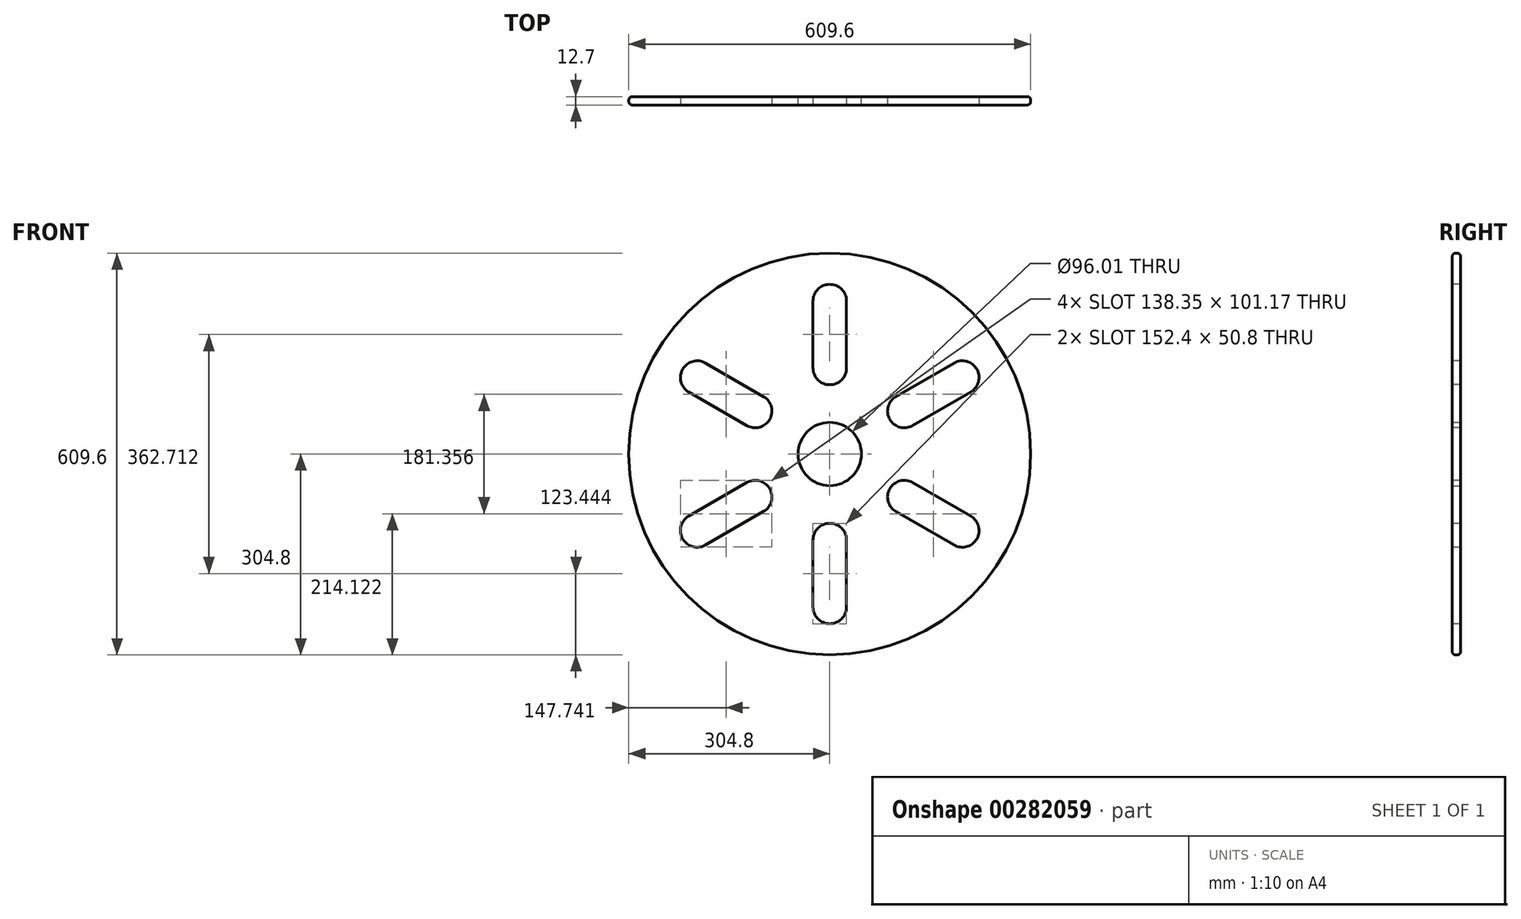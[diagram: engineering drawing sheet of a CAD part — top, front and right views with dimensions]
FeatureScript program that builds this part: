
annotation { "Feature Type Name" : "Feature", "Feature Type Description" : "" }
export const myFeature = defineFeature(function(context is Context, id is Id, definition is map)
    precondition{}
    {
        {
            var Q0;
            Q0=qCreatedBy(makeId("Front.planeOp"),FACE);
            var sketch = newSketch(context, id + "F0", { "sketchPlane" : qUnion([Q0])});
            skCircle(sketch, "E0", {"center": v(0, 0) * mm, "radius": 304.8 * mm});
            skCircle(sketch, "E1", {"center": v(0, 0) * mm, "radius": 48 * mm});
            skSolve(sketch);
        }
        {
            var Q0;
            Q0=makeQuery(id+"F0.imprint","IMPRINT",FACE,{"disambiguationData":[TD([[makeQuery(id+"F0.imprint","IMPRINT",EDGE,{"derivedFrom":sQuery(id+"F0.wireOp",EDGE,"E0")}),1.0]])]});
            extrude(context, id + "F1", {"entities" : qUnion([Q0]), "depth" : 12.7 * mm});
        }
        {
            var Q0;
            Q0=makeQuery(id+"F1.opExtrude","CAP_FACE",FACE,{"disambiguationData":[OSD([sQuery(id+"F0.wireOp",EDGE,"E0"),sQuery(id+"F0.wireOp",EDGE,"E1")])],"isStart":false});
            var sketch = newSketch(context, id + "F2", { "sketchPlane" : qUnion([Q0])});
            skLineSegment(sketch, "E2.left", {"start": v(-25.4, 130.56) * mm, "end": v(-25.4, 232.16) * mm});
            skLineSegment(sketch, "E2.right", {"start": v(25.4, 130.56) * mm, "end": v(25.4, 232.16) * mm});
            skPoint(sketch, "E2.middle", {"position": v(0, 181.36) * mm});
            skArc(sketch, "E3", {"start": v(25.4, 232.16) * mm, "mid": v(0, 257.56) * mm, "end": v(-25.4, 232.16) * mm});
            skArc(sketch, "E4", {"start": v(-25.4, 130.56) * mm, "mid": v(0, 105.16) * mm, "end": v(25.4, 130.56) * mm});
            skArc(sketch, "E5.1.0", {"start": v(-125.76, 43.28) * mm, "mid": v(-91.07, 52.58) * mm, "end": v(-100.36, 87.28) * mm});
            skLineSegment(sketch, "E5.1.1", {"start": v(-100.36, 87.28) * mm, "end": v(-188.35, 138.08) * mm});
            skLineSegment(sketch, "E5.1.2", {"start": v(-125.76, 43.28) * mm, "end": v(-213.75, 94.08) * mm});
            skArc(sketch, "E5.1.3", {"start": v(-188.35, 138.08) * mm, "mid": v(-223.05, 128.78) * mm, "end": v(-213.75, 94.08) * mm});
            skArc(sketch, "E5.2.0", {"start": v(-100.36, -87.28) * mm, "mid": v(-91.07, -52.58) * mm, "end": v(-125.76, -43.28) * mm});
            skLineSegment(sketch, "E5.2.1", {"start": v(-125.76, -43.28) * mm, "end": v(-213.75, -94.08) * mm});
            skLineSegment(sketch, "E5.2.2", {"start": v(-100.36, -87.28) * mm, "end": v(-188.35, -138.08) * mm});
            skArc(sketch, "E5.2.3", {"start": v(-213.75, -94.08) * mm, "mid": v(-223.05, -128.78) * mm, "end": v(-188.35, -138.08) * mm});
            skArc(sketch, "E5.3.0", {"start": v(25.4, -130.56) * mm, "mid": v(0, -105.16) * mm, "end": v(-25.4, -130.56) * mm});
            skLineSegment(sketch, "E5.3.1", {"start": v(-25.4, -130.56) * mm, "end": v(-25.4, -232.16) * mm});
            skLineSegment(sketch, "E5.3.2", {"start": v(25.4, -130.56) * mm, "end": v(25.4, -232.16) * mm});
            skArc(sketch, "E5.3.3", {"start": v(-25.4, -232.16) * mm, "mid": v(0, -257.56) * mm, "end": v(25.4, -232.16) * mm});
            skArc(sketch, "E5.4.0", {"start": v(125.76, -43.28) * mm, "mid": v(91.07, -52.58) * mm, "end": v(100.36, -87.28) * mm});
            skLineSegment(sketch, "E5.4.1", {"start": v(100.36, -87.28) * mm, "end": v(188.35, -138.08) * mm});
            skLineSegment(sketch, "E5.4.2", {"start": v(125.76, -43.28) * mm, "end": v(213.75, -94.08) * mm});
            skArc(sketch, "E5.4.3", {"start": v(188.35, -138.08) * mm, "mid": v(223.05, -128.78) * mm, "end": v(213.75, -94.08) * mm});
            skArc(sketch, "E5.5.0", {"start": v(100.36, 87.28) * mm, "mid": v(91.07, 52.58) * mm, "end": v(125.76, 43.28) * mm});
            skLineSegment(sketch, "E5.5.1", {"start": v(125.76, 43.28) * mm, "end": v(213.75, 94.08) * mm});
            skLineSegment(sketch, "E5.5.2", {"start": v(100.36, 87.28) * mm, "end": v(188.35, 138.08) * mm});
            skArc(sketch, "E5.5.3", {"start": v(213.75, 94.08) * mm, "mid": v(223.05, 128.78) * mm, "end": v(188.35, 138.08) * mm});
            skPoint(sketch, "E5.center", {"position": v(0, 0) * mm});
            skLineSegment(sketch, "E6", {"start": v(0, 304.8) * mm, "end": v(0, -304.8) * mm, "construction": true});
            skSolve(sketch);
        }
        {
            var Q0;
            Q0=makeQuery(id+"F2.imprint","IMPRINT",FACE,{"disambiguationData":[TD([[makeQuery(id+"F2.imprint","IMPRINT",EDGE,{"derivedFrom":sQuery(id+"F2.wireOp",EDGE,"E2.left")}),-1.0]])]});
            var Q1;
            Q1=makeQuery(id+"F2.imprint","IMPRINT",FACE,{"disambiguationData":[TD([[makeQuery(id+"F2.imprint","IMPRINT",EDGE,{"derivedFrom":sQuery(id+"F2.wireOp",EDGE,"E5.5.0")}),1.0]])]});
            var Q2;
            Q2=makeQuery(id+"F2.imprint","IMPRINT",FACE,{"disambiguationData":[TD([[makeQuery(id+"F2.imprint","IMPRINT",EDGE,{"derivedFrom":sQuery(id+"F2.wireOp",EDGE,"E5.4.0")}),1.0]])]});
            var Q3;
            Q3=makeQuery(id+"F2.imprint","IMPRINT",FACE,{"disambiguationData":[TD([[makeQuery(id+"F2.imprint","IMPRINT",EDGE,{"derivedFrom":sQuery(id+"F2.wireOp",EDGE,"E5.3.0")}),1.0]])]});
            var Q4;
            Q4=makeQuery(id+"F2.imprint","IMPRINT",FACE,{"disambiguationData":[TD([[makeQuery(id+"F2.imprint","IMPRINT",EDGE,{"derivedFrom":sQuery(id+"F2.wireOp",EDGE,"E5.2.0")}),1.0]])]});
            var Q5;
            Q5=makeQuery(id+"F2.imprint","IMPRINT",FACE,{"disambiguationData":[TD([[makeQuery(id+"F2.imprint","IMPRINT",EDGE,{"derivedFrom":sQuery(id+"F2.wireOp",EDGE,"E5.1.0")}),1.0]])]});
            extrude(context, id + "F3", {"entities" : qUnion([Q0, Q1, Q2, Q3, Q4, Q5]), "operationType" : NewBodyOperationType.REMOVE, "endBound" : BoundingType.THROUGH_ALL, "oppositeDirection" : true, "depth" : 25.4 * mm});
        }
        {
            var Q0;
            Q0=makeQuery(id+"F1.opExtrude","CAP_EDGE",EDGE,{"disambiguationData":[OSD([sQuery(id+"F0.wireOp",EDGE,"E0")])],"isStart":true});
            var Q1;
            Q1=makeQuery(id+"F1.opExtrude","CAP_EDGE",EDGE,{"disambiguationData":[OSD([sQuery(id+"F0.wireOp",EDGE,"E0")])],"isStart":false});
            fillet(context, id + "F4", {"entities" : qUnion([Q0, Q1]), "radius" : 5.08 * mm, "tangentPropagation" : true, "allowEdgeOverflow" : false});
        }
    });
